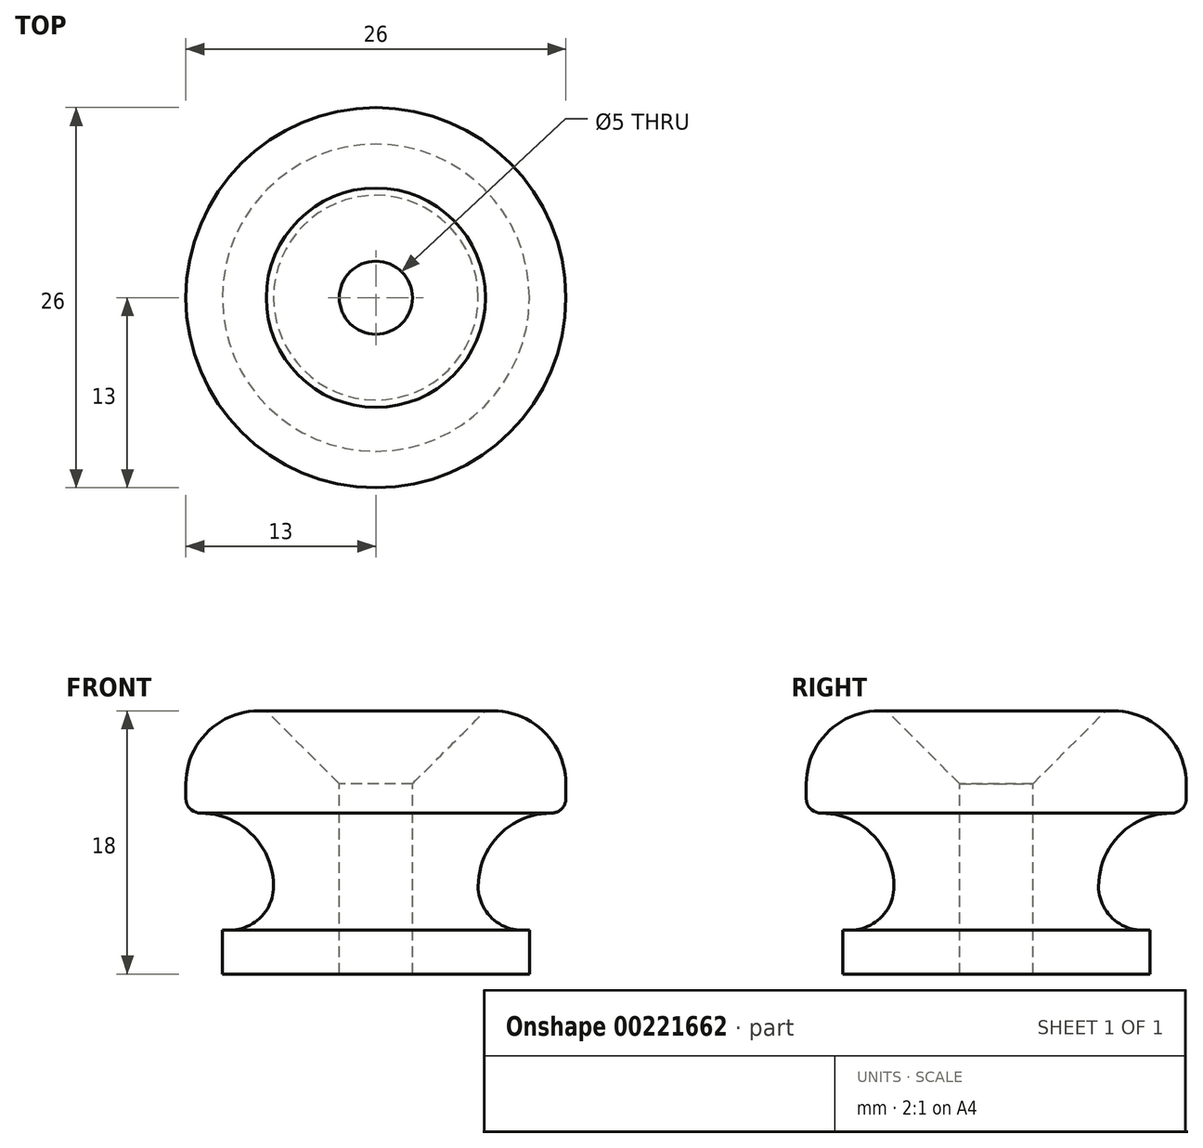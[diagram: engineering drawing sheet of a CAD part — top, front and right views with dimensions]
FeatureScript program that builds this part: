
annotation { "Feature Type Name" : "Feature", "Feature Type Description" : "" }
export const myFeature = defineFeature(function(context is Context, id is Id, definition is map)
    precondition{}
    {
        {
            var Q0;
            Q0=qCreatedBy(makeId("Front.planeOp"),FACE);
            var sketch = newSketch(context, id + "F0", { "sketchPlane" : qUnion([Q0])});
            skLineSegment(sketch, "E0", {"start": v(-2.5, 0) * mm, "end": v(-2.5, 15) * mm});
            skLineSegment(sketch, "E1", {"start": v(-2.5, 15) * mm, "end": v(-8, 15) * mm});
            skLineSegment(sketch, "E2", {"start": v(-13, 10) * mm, "end": v(-13, 8) * mm});
            skLineSegment(sketch, "E3", {"start": v(-13, 8) * mm, "end": v(-12, 8) * mm});
            skLineSegment(sketch, "E4", {"start": v(-7, 3) * mm, "end": v(-7, 3) * mm});
            skLineSegment(sketch, "E5", {"start": v(-7, 0) * mm, "end": v(-2.5, 0) * mm});
            skLineSegment(sketch, "E6", {"start": v(0, 11.4) * mm, "end": v(0, -4.9) * mm, "construction": true});
            skPoint(sketch, "E7.visualSharp", {"position": v(-7, 8) * mm});
            skArc(sketch, "E7.filletArc", {"start": v(-7, 3) * mm, "mid": v(-8.46, 6.54) * mm, "end": v(-12, 8) * mm});
            skPoint(sketch, "E8.visualSharp", {"position": v(-13, 15) * mm});
            skArc(sketch, "E8.filletArc", {"start": v(-8, 15) * mm, "mid": v(-11.54, 13.54) * mm, "end": v(-13, 10) * mm});
            skLineSegment(sketch, "E9", {"start": v(-10, 0) * mm, "end": v(-10.5, 0) * mm});
            skLineSegment(sketch, "E10", {"start": v(-10.5, 0) * mm, "end": v(-10.5, -3) * mm});
            skLineSegment(sketch, "E11", {"start": v(-10.5, -3) * mm, "end": v(-2.5, -3) * mm});
            skLineSegment(sketch, "E12", {"start": v(-2.5, -3) * mm, "end": v(-2.5, 0) * mm});
            skPoint(sketch, "E13.visualSharp", {"position": v(-7, 0) * mm});
            skArc(sketch, "E13.filletArc", {"start": v(-10, 0) * mm, "mid": v(-7.88, 0.88) * mm, "end": v(-7, 3) * mm});
            skSolve(sketch);
        }
        {
            var Q0;
            Q0=makeQuery(id+"F0.imprint","IMPRINT",FACE,{"disambiguationData":[TD([[makeQuery(id+"F0.imprint","IMPRINT",EDGE,{"derivedFrom":sQuery(id+"F0.wireOp",EDGE,"E0")}),1.0]])]});
            var Q1;
            Q1=sQuery(id+"F0.wireOp",EDGE,"E6");
            revolve(context, id + "F1", {"entities" : qUnion([Q0]), "axis" : qUnion([Q1]), "revolveType" : RevolveType.FULL});
        }
        {
            var Q0;
            Q0=makeQuery(id+"F1.opRevolve","SWEPT_EDGE",EDGE,{"disambiguationData":[OSD([sQuery(id+"F0.wireOp",EDGE,"E0"),sQuery(id+"F0.wireOp",EDGE,"E1")])]});
            chamfer(context, id + "F2", {"entities" : qUnion([Q0]), "width" : 5 * mm, "tangentPropagation" : true});
        }
        {
            var Q0;
            Q0=makeQuery(id+"F1.opRevolve","SWEPT_EDGE",EDGE,{"disambiguationData":[OSD([sQuery(id+"F0.wireOp",EDGE,"E2"),sQuery(id+"F0.wireOp",EDGE,"E3")])]});
            fillet(context, id + "F3", {"entities" : qUnion([Q0]), "radius" : 1 * mm, "tangentPropagation" : true, "allowEdgeOverflow" : false});
        }
    });
